# Revit family: Domotics-DomesticRanges-GEWISS-SYSTEM_COMMAND-ONE-WAY_SWITCH_KEY
name_source: partatom
category: Apparecchi elettrici
revit_build: Autodesk Revit 2016 (Build: 20161004_0715(x64)
units: mm (PartAtom-declared; Revit-internal decimal feet)

## family parameters
Condiviso = Sì
Host = Superficie
Mantenere orientamento annotazione = Sì
Numero OmniClass = 23.80.50.11.14
Punto di calcolo locali = Sì
Quota connettore circolare = Usa diametro
Taglio con vuoti quando caricato = No
Tipo di parte = Normale
Titolo OmniClass = Switches

## types (2) — shared parameters
Button key = With key
Carico apparente = 0 VA
Catalogue = DOMOTICS
Catalogue Range = SYSTEM - DOMESTIC RANGE
Characteristics = 2P - 10AX
Description. = One-way switch (2P)
Description: = 2P - 10AX
Electrocod = 0130
IDF = 46e1c4a7-1b6e-47e8-9bb1-a477be4951b1
IDT = 4eb9a7d3-e0a4-4258-a2b7-f9de543542f9
Immagine tipo = gw21005.jpg
N. poli = 1
No. SYSTEM modules = 1
Produttore = GEWISS S.p.A.
Prospetto di default = 1219 mm
Pulsante = GEWISS NERO
SEO = 1 way switch
Simbolo_ = SIMBOLO INTERRUTTORI : INTCHIAVE
Technical sheet = https://www.gewiss.com
Type = With key
Typology = With key
URL = https://www.gewiss.com
Version file RFA = 19.4
Volt = 230 V
Voltage = 250 V ac
Voltage: = 250 V ac

## per-type parameters (varying)
| type | Colour | Descrizione | EAN code | Modello |
| GW20005 - Key-operated switch-2P 10A white | White | KEY-OPERATED SWITCH-2P 10A SY/WT | 8011564000056 | GW20005 |
| GW21005 - Key-operated switch-2P 10A black | Black | KEY-OPERATED SWITCH-2P 10A SY/BK | 8011564127982 | GW21005 |
